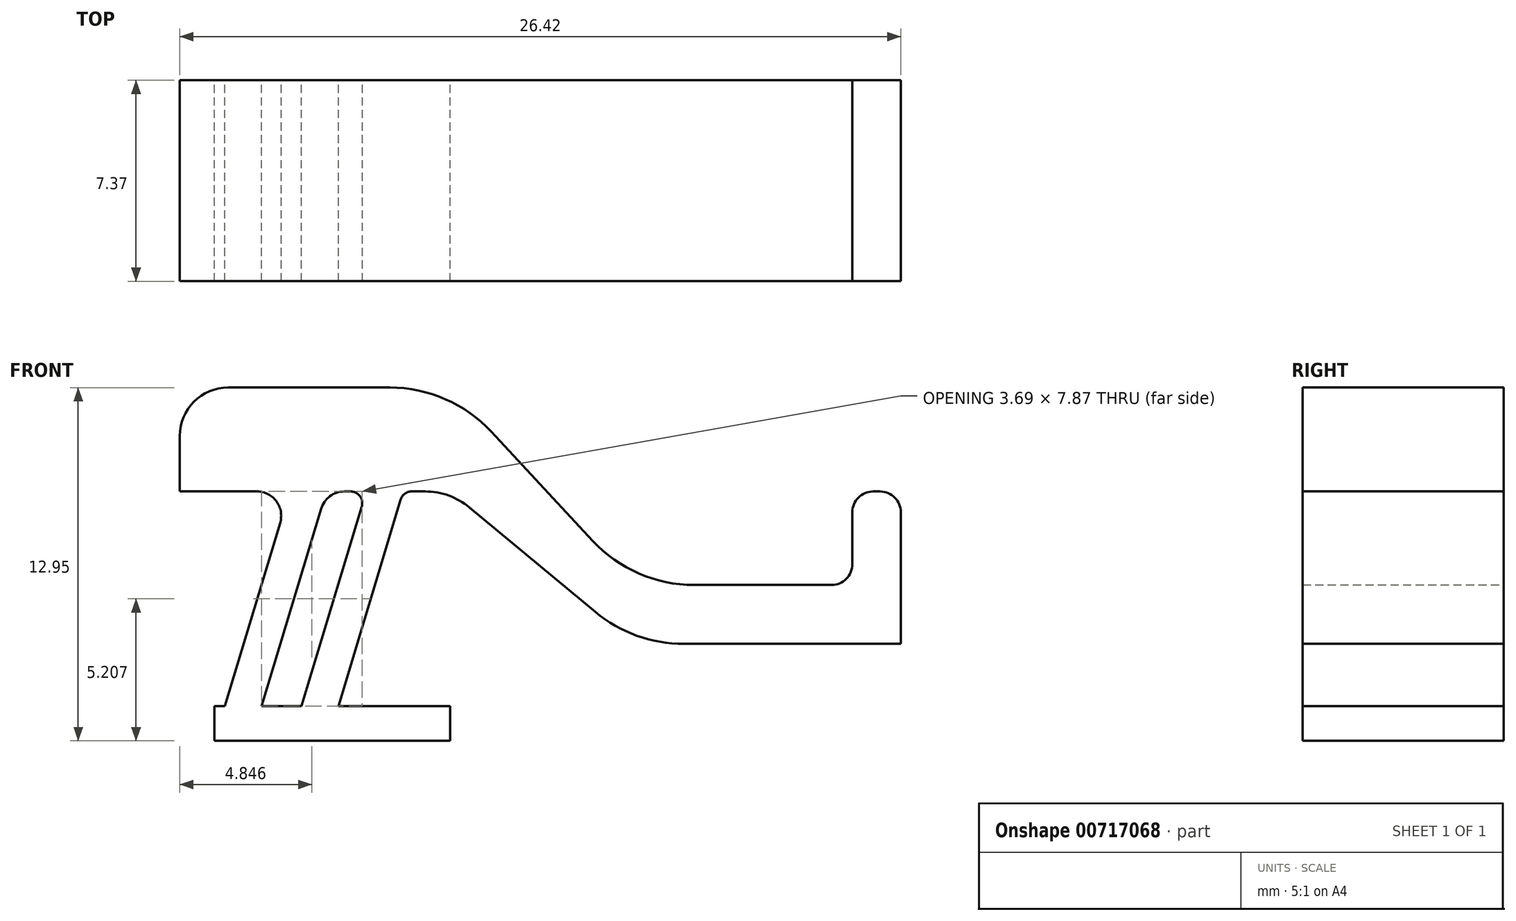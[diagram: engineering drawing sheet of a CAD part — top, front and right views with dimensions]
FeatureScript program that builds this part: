
annotation { "Feature Type Name" : "Feature", "Feature Type Description" : "" }
export const myFeature = defineFeature(function(context is Context, id is Id, definition is map)
    precondition{}
    {
        {
            var Q0;
            Q0=qCreatedBy(makeId("Front.planeOp"),FACE);
            var sketch = newSketch(context, id + "F0", { "sketchPlane" : qUnion([Q0])});
            skLineSegment(sketch, "E0.bottom", {"start": v(-8.13, 12.95) * mm, "end": v(-2.21, 12.95) * mm});
            skLineSegment(sketch, "E0.top", {"start": v(-8.64, 0) * mm, "end": v(0, 0) * mm});
            skLineSegment(sketch, "E0.left", {"start": v(-8.64, 12.88) * mm, "end": v(-8.64, 9.14) * mm});
            skLineSegment(sketch, "E0.right", {"start": v(0, 12.45) * mm, "end": v(0, 9.14) * mm});
            skLineSegment(sketch, "E1.bottom", {"start": v(-2.21, 12.95) * mm, "end": v(-8.13, 12.95) * mm});
            skLineSegment(sketch, "E1.top", {"start": v(-7.08, 9.14) * mm, "end": v(-9.9, 9.14) * mm});
            skLineSegment(sketch, "E1.left", {"start": v(0, 12.45) * mm, "end": v(0, 9.14) * mm, "construction": true});
            skLineSegment(sketch, "E1.right", {"start": v(-9.9, 11.18) * mm, "end": v(-9.9, 9.14) * mm});
            skPoint(sketch, "E2.visualSharp", {"position": v(-9.9, 12.95) * mm});
            skArc(sketch, "E2.filletArc", {"start": v(-8.13, 12.95) * mm, "mid": v(-9.39, 12.43) * mm, "end": v(-9.9, 11.18) * mm});
            skLineSegment(sketch, "E3", {"start": v(8.56, 3.56) * mm, "end": v(10.44, 3.56) * mm});
            skLineSegment(sketch, "E4", {"start": v(-8.25, 1.27) * mm, "end": v(-6.23, 8) * mm});
            skLineSegment(sketch, "E5", {"start": v(-6.9, 1.27) * mm, "end": v(-4.73, 8.51) * mm});
            skLineSegment(sketch, "E6", {"start": v(-5.44, 1.27) * mm, "end": v(-3.24, 8.6) * mm});
            skLineSegment(sketch, "E7", {"start": v(-4.1, 1.27) * mm, "end": v(-1.82, 8.84) * mm});
            skLineSegment(sketch, "E8", {"start": v(-7.26, 4.57) * mm, "end": v(-5.91, 4.57) * mm, "construction": true});
            skLineSegment(sketch, "E9", {"start": v(-4.45, 4.57) * mm, "end": v(-3.1, 4.57) * mm, "construction": true});
            skPoint(sketch, "E10.newPointA", {"position": v(-5.88, 9.14) * mm});
            skArc(sketch, "E10.filletArc", {"start": v(-6.23, 8) * mm, "mid": v(-6.37, 8.79) * mm, "end": v(-7.08, 9.14) * mm});
            skLineSegment(sketch, "E11", {"start": v(-3.88, 9.14) * mm, "end": v(-3.65, 9.14) * mm});
            skPoint(sketch, "E12.visualSharp", {"position": v(-4.54, 9.14) * mm});
            skArc(sketch, "E12.filletArc", {"start": v(-3.88, 9.14) * mm, "mid": v(-4.4, 8.97) * mm, "end": v(-4.73, 8.51) * mm});
            skPoint(sketch, "E13.visualSharp", {"position": v(-3.07, 9.14) * mm});
            skArc(sketch, "E13.filletArc", {"start": v(-3.24, 8.6) * mm, "mid": v(-3.3, 8.97) * mm, "end": v(-3.65, 9.14) * mm});
            skLineSegment(sketch, "E14", {"start": v(-1.4, 9.14) * mm, "end": v(-0.92, 9.14) * mm});
            skPoint(sketch, "E15.visualSharp", {"position": v(-1.73, 9.14) * mm});
            skArc(sketch, "E15.filletArc", {"start": v(-1.4, 9.14) * mm, "mid": v(-1.66, 9.06) * mm, "end": v(-1.82, 8.84) * mm});
            skLineSegment(sketch, "E16", {"start": v(-8.64, 1.27) * mm, "end": v(0, 1.27) * mm});
            skPoint(sketch, "E17.orphan", {"position": v(-7.29, 0) * mm});
            skPoint(sketch, "E18.orphan", {"position": v(-5.82, 0) * mm});
            skPoint(sketch, "E19.orphan", {"position": v(-4.48, 0) * mm});
            skLineSegment(sketch, "E20.trimOffspring", {"start": v(-8.64, 1.27) * mm, "end": v(-8.64, 0) * mm});
            skLineSegment(sketch, "E21.trimOffspring", {"start": v(0, 1.27) * mm, "end": v(0, 0) * mm});
            skLineSegment(sketch, "E22", {"start": v(0.7, 8.56) * mm, "end": v(5.32, 4.73) * mm});
            skPoint(sketch, "E23.visualSharp", {"position": v(0, 9.14) * mm});
            skArc(sketch, "E23.filletArc", {"start": v(0.7, 8.56) * mm, "mid": v(-0.05, 9) * mm, "end": v(-0.92, 9.14) * mm});
            skLineSegment(sketch, "E24", {"start": v(1.5, 11.33) * mm, "end": v(5.22, 7.34) * mm});
            skLineSegment(sketch, "E25", {"start": v(6.73, 3.56) * mm, "end": v(6.73, 5.72) * mm, "construction": true});
            skPoint(sketch, "E26.visualSharp", {"position": v(0, 12.95) * mm});
            skArc(sketch, "E26.filletArc", {"start": v(1.5, 11.33) * mm, "mid": v(-0.18, 12.53) * mm, "end": v(-2.21, 12.95) * mm});
            skPoint(sketch, "E27.visualSharp", {"position": v(6.73, 3.56) * mm});
            skArc(sketch, "E27.filletArc", {"start": v(5.32, 4.73) * mm, "mid": v(6.84, 3.86) * mm, "end": v(8.56, 3.56) * mm});
            skLineSegment(sketch, "E28", {"start": v(8.94, 5.72) * mm, "end": v(10.44, 5.72) * mm});
            skLineSegment(sketch, "E29", {"start": v(10.44, 3.56) * mm, "end": v(10.44, 5.72) * mm, "construction": true});
            skPoint(sketch, "E30.visualSharp", {"position": v(6.73, 5.72) * mm});
            skArc(sketch, "E30.filletArc", {"start": v(5.22, 7.34) * mm, "mid": v(6.91, 6.14) * mm, "end": v(8.94, 5.72) * mm});
            skLineSegment(sketch, "E31", {"start": v(16.51, 8.38) * mm, "end": v(16.51, 3.56) * mm});
            skLineSegment(sketch, "E32", {"start": v(10.44, 3.56) * mm, "end": v(16.51, 3.56) * mm});
            skLineSegment(sketch, "E33", {"start": v(15.75, 9.14) * mm, "end": v(15.5, 9.14) * mm});
            skLineSegment(sketch, "E34", {"start": v(14.73, 8.38) * mm, "end": v(14.73, 6.48) * mm});
            skLineSegment(sketch, "E35", {"start": v(13.97, 5.72) * mm, "end": v(10.44, 5.72) * mm});
            skPoint(sketch, "E36.visualSharp", {"position": v(16.51, 9.14) * mm});
            skArc(sketch, "E36.filletArc", {"start": v(16.51, 8.38) * mm, "mid": v(16.29, 8.92) * mm, "end": v(15.75, 9.14) * mm});
            skPoint(sketch, "E37.visualSharp", {"position": v(14.73, 9.14) * mm});
            skArc(sketch, "E37.filletArc", {"start": v(15.5, 9.14) * mm, "mid": v(14.96, 8.92) * mm, "end": v(14.73, 8.38) * mm});
            skPoint(sketch, "E38.visualSharp", {"position": v(14.73, 5.72) * mm});
            skArc(sketch, "E38.filletArc", {"start": v(13.97, 5.72) * mm, "mid": v(14.5, 5.94) * mm, "end": v(14.73, 6.48) * mm});
            skSolve(sketch);
        }
        {
            var Q0;
            Q0 = qSketchRegion(id + "F0", true);
            extrude(context, id + "F1", {"entities" : qUnion([Q0]), "depth" : 7.37 * mm, "offsetDistance" : 25.4 * mm});
        }
    });
